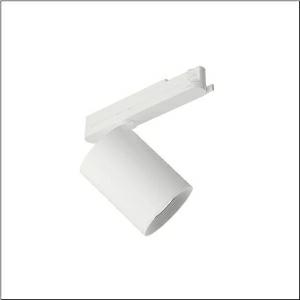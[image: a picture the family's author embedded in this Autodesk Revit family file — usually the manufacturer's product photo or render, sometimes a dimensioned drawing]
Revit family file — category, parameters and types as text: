
# Revit family: spot_21_51se13dbd5b
name_source: partatom
category: Lighting Fixtures
units: mm (PartAtom-declared; Revit-internal decimal feet)

## family parameters
Cut with Voids When Loaded = No
Host = Face
Light Source = No
Part Type = Normal
Room Calculation Point = No
Round Connector Dimension = Use Diameter
Shared = No

## types (1)
- --- (1 x LED, 5410 lm, 42.1 W, 4000K)
    Apparent Load = 42 VA
    CIE Flux Codes = 95 98 99 100 100
    Color Rendering = 90
    Color Temperature = 4000K
    Default Elevation = 1800 mm
    Description = Spot 21, directional spotlight, light control with lens, of PMMA, LED rated luminous flux: 5.200lm, light colour: 940, control gear: ECG Multilumen, with 3-phase adapter, mains connection: 220..240V, AC, 50/60Hz, of aluminium, traffic white (RAL 9016), length: 253mm, diameter: 105mm, protection rating (complete): IP20, insulation class (complete): insulation class I (protective earthing), certification: CE, impact resistance: IK02, permissible ambient temperature for indoor applications: -20..+40°C, packaging unit: 1 piece
    Height = 175 mm
    Lamp = 1 x LED
    Lamp Light Flux = 5410 lm
    Lamp Power = 42.1 W
    Lamp count = 1
    Length = 105 mm
    Luminous efficacy = 129 lm/W
    Manufacturer = Siteco
    ModVariant = No
    Model = 51SE13DBD5B
    Mounting Place = Ceiling
    Mounting Type = Pendant
    Number of Poles = 1
    OnlyDefault = Yes
    Power Factor = 1
    Product Name = Spot 21
    Product group = directional spotlight
    ProductGroupID = 905
    Protection Class = Protection class I
    Protection Degree = IP 20
    RLX_Detail_Level = 1
    RLX_Emergency_Light_Flux = 0 lm
    RLX_Emergency_Type = 0
    RLX_Emergency_Type_DB = No
    RlxData = <blob elided: 17689 chars, md5=36fd1013>
    Socket = socket
    Standby Power = 0 W
    System Light Flux = 5410 lm
    System Power = 42 W
    Type Comments = factory setting: luminous flux: 100 % | (ON | ON | ON | ON) | 1050 mA
    Type Image = l_1003976.jpg
    URL = http://relux.com
    VarID = @adj_165569
    Voltage = 0 V
    Weight = 0.00 kg
    Width = 0 mm  [stored 0 ft]

note: [stored X ft] marks values corroborated as IEEE doubles in the binary element streams (Revit-internal decimal feet)

## geometry (parser evidence)
native form markers: Blend x4, Sweep x11
no freeform markers — native parametric forms only
